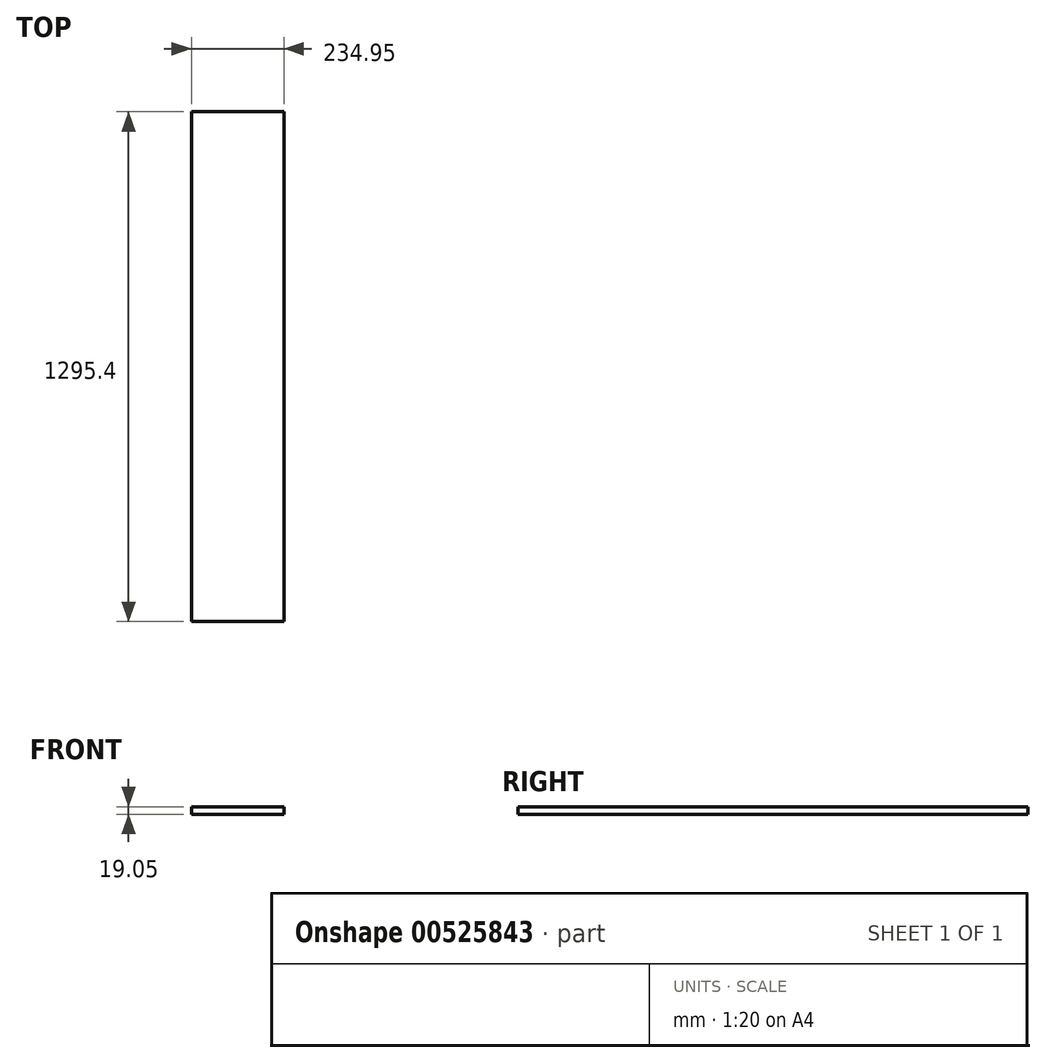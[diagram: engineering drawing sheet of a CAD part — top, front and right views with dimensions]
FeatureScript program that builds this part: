
annotation { "Feature Type Name" : "Feature", "Feature Type Description" : "" }
export const myFeature = defineFeature(function(context is Context, id is Id, definition is map)
    precondition{}
    {
        {
            var Q0;
            Q0=qCreatedBy(makeId("Front.planeOp"),FACE);
            var sketch = newSketch(context, id + "F0", { "sketchPlane" : qUnion([Q0])});
            skLineSegment(sketch, "E0.top", {"start": v(0, 19.05) * mm, "end": v(234.95, 19.05) * mm});
            skLineSegment(sketch, "E0.right", {"start": v(234.95, 0) * mm, "end": v(234.95, 19.05) * mm});
            skLineSegment(sketch, "E1", {"start": v(0, 0) * mm, "end": v(234.95, 0) * mm});
            skLineSegment(sketch, "E2", {"start": v(0, 0) * mm, "end": v(0, 19.05) * mm});
            skSolve(sketch);
        }
        {
            var Q0;
            Q0=qSketchRegion(id+"F0",true);
            extrude(context, id + "F1", {"entities" : qUnion([Q0]), "depth" : 1295.4 * mm, "offsetDistance" : 25.4 * mm});
        }
    });
